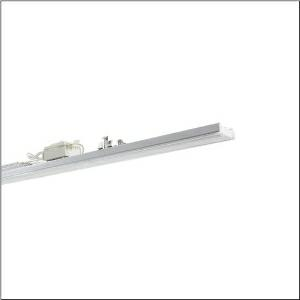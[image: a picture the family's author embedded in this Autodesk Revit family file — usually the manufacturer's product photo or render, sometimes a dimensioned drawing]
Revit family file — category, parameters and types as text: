
# Revit family: licross_r__11_recessed_mo_51tl11cn49xg_3399
name_source: partatom
category: Lighting Fixtures
units: mm (PartAtom-declared; Revit-internal decimal feet)

## family parameters
Cut with Voids When Loaded = No
Host = Face
Light Source = No
Part Type = Normal
Room Calculation Point = No
Round Connector Dimension = Use Diameter
Shared = No

## types (1)
- --- (1 x LED, 9160 lm, 49.3 W, 4000K)
    Apparent Load = 49 VA
    CIE Flux Codes = 89 96 99 100 100
    Color Rendering = 80
    Color Temperature = 4000K
    Default Elevation = 1800 mm
    Description = Licross® 11 Recessed MO, luminaire insert, of sheet steel, coil coated, white, length: 1.500mm, width: 66mm, height: 67mm, LED rated luminous flux: 9.160lm, light colour: 840, control gear: ON/OFF Multilumen, CLOi, with plug, 3-pole, with phase selection, mains connection: 220..240V, AC, 50/60Hz, start of lifetime: 49W, end of service life: 55W, halogen-free wiring, primary light control with lens, of plastic, primary optical cover: cover, of PMMA, light emission: direct distribution, primary light characteristic: symmetric, protection rating (complete): IP40, insulation class (complete): insulation class I (protective earthing), certification: CE, ENEC, VDE, UKCA, protection symbol: D if used in an environment without relevant dust loads with corresponding accessories, impact resistance: IK06, permissible ambient temperature for indoor applications: -35..+40°C, corresponds to IFS (International Featured Standards) requirements for safety and quality in the food industry, reducing of maximum allowable ambient temperature of 5°C with ceiling mounting, LABS conformity tested according to VDMA 24364:2018-05, packaging unit: 1 piece
    Height = 58 mm
    Lamp = 1 x LED
    Lamp Light Flux = 9160 lm
    Lamp Power = 49.3 W
    Lamp count = 1
    Length = 1500 mm
    Luminous efficacy = 186 lm/W
    Manufacturer = Siteco
    ModVariant = No
    Model = 51TL11CN49XG
    Mounting Place = Ceiling
    Mounting Type = Pendant
    Number of Poles = 1
    OnlyDefault = Yes
    Power Factor = 1
    Product Name = Licross® 11 Recessed MO
    Product group = luminaire insert
    ProductGroupID = 902
    Protection Class = Protection class I
    Protection Degree = IP 40
    RLX_Detail_Level = 1
    RLX_Emergency_Light_Flux = 0 lm
    RLX_Emergency_Type = 0
    RLX_Emergency_Type_DB = No
    RlxData = <blob elided: 22289 chars, md5=010f5a22>
    Socket = socket
    Standby Power = 0 W
    System Light Flux = 9160 lm
    System Power = 49 W
    Type Comments = factory setting: luminous flux: 100 % | (A | C | E) | 113 mA
    Type Image = l_1296930.jpg
    URL = http://relux.com
    VarID = @adj_084466
    Voltage = 0 V
    Weight = 0.00 kg
    Width = 66 mm

## geometry (parser evidence)
native form markers: Blend x4, Sweep x11
no freeform markers — native parametric forms only
